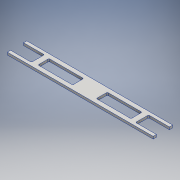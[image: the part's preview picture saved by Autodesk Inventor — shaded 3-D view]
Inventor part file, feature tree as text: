
AUTODESK INVENTOR PART (.ipt)
format: ipt  version: 2016 (Build 200138000, 138)  size: 143,872 bytes
history: native  units: mm
features: extrude x1, sketch x1
ambient origin geometry x8: Origin, YZ Plane, XZ Plane, XY Plane, X Axis, Y Axis, Z Axis, Center Point
bodies: Solid1 (feature_tree)
feature tree (2):
  extrude  "Extrusion1"  Depth=43.104285mm
  sketch  "Sketch1"  dims[d44=135.4582mm d45=43.104285mm d46=16.546659mm d47=16.529mm d48=21.585333mm d58=92.185791mm d59=9.525mm d60=0.0mm]
